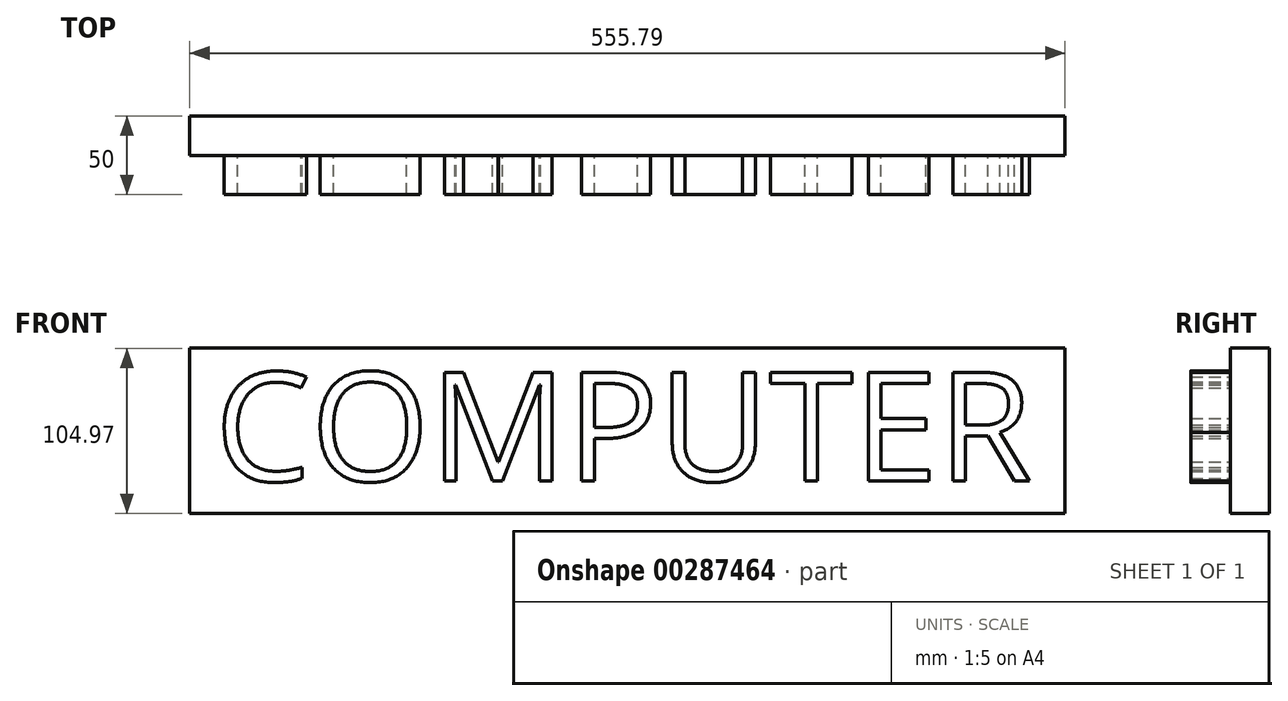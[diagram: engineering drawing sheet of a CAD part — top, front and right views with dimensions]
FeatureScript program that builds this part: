
annotation { "Feature Type Name" : "Feature", "Feature Type Description" : "" }
export const myFeature = defineFeature(function(context is Context, id is Id, definition is map)
    precondition{}
    {
        {
            var Q0;
            Q0=qCreatedBy(makeId("Front.planeOp"),FACE);
            var sketch = newSketch(context, id + "F0", { "sketchPlane" : qUnion([Q0])});
            skLineSegment(sketch, "E0.bottom", {"start": v(0, 0) * mm, "end": v(555.79, 0) * mm});
            skLineSegment(sketch, "E0.top", {"start": v(0, 104.97) * mm, "end": v(555.79, 104.97) * mm});
            skLineSegment(sketch, "E0.left", {"start": v(0, 0) * mm, "end": v(0, 104.97) * mm});
            skLineSegment(sketch, "E0.right", {"start": v(555.79, 0) * mm, "end": v(555.79, 104.97) * mm});
            skSolve(sketch);
        }
        {
            var Q0;
            Q0=qCreatedBy(makeId("Front.planeOp"),FACE);
            var sketch = newSketch(context, id + "F1", { "sketchPlane" : qUnion([Q0])});
            skText(sketch, "E1", { "text": "COMPUTER", "fontName": "OpenSans-Regular.ttf"});
            const initialGuessF1  = {"E1": [0.01597, 0.02059, 1, 0, 0.06957]};
            skSetInitialGuess(sketch, initialGuessF1);
            skSolve(sketch);
        }
        {
            var Q0;
            Q0=qSketchRegion(id+"F0",true);
            extrude(context, id + "F2", {"entities" : qUnion([Q0]), "oppositeDirection" : true, "depth" : 25 * mm});
        }
        {
            var Q0;
            Q0=qSketchRegion(id+"F1",true);
            extrude(context, id + "F3", {"entities" : qUnion([Q0]), "operationType" : NewBodyOperationType.ADD, "depth" : 25 * mm});
        }
    });
